FCSTD DOCUMENT  (FreeCAD 0.15R4671 (Git))
Label: OpenFacedCheeks
License: All rights reserved
LicenseURL: http://en.wikipedia.org/wiki/All_rights_reserved
objects: Sketcher::SketchObject×1
note: 1 computed .brp shape members not serialized (recipe doc carries the construction recipe); baked Part::Feature solids carry a one-line shape summary decoded from their .brp

FEATURE [Sketcher::SketchObject] Sketch
  sketch-geometry (18):
    g0: LineSegment StartX=0 StartY=0 StartZ=0 EndX=0 EndY=120.65 EndZ=0
    g1: LineSegment StartX=0 StartY=0 StartZ=0 EndX=285.75 EndY=0 EndZ=0
    g2: LineSegment StartX=285.75 StartY=0 StartZ=0 EndX=285.75 EndY=40.64 EndZ=0
    g3: LineSegment StartX=9.525 StartY=9.525 StartZ=0 EndX=276.225 EndY=9.525 EndZ=0
    g4: LineSegment StartX=9.525 StartY=9.525 StartZ=0 EndX=9.525 EndY=107.371 EndZ=0
    g5: LineSegment StartX=276.225 StartY=9.525 StartZ=0 EndX=276.225 EndY=34.925 EndZ=0
    g6: LineSegment StartX=276.225 StartY=34.925 StartZ=0 EndX=123.825 EndY=34.925 EndZ=0
    g7: LineSegment StartX=9.525 StartY=107.371 StartZ=0 EndX=17.241 EndY=101.786 EndZ=0
    g8: LineSegment StartX=17.241 StartY=101.786 StartZ=0 EndX=22.8257 EndY=109.502 EndZ=0
    g9: LineSegment StartX=22.8257 StartY=109.502 StartZ=0 EndX=89.6981 EndY=61.1019 EndZ=0
    g10: LineSegment StartX=89.6981 StartY=61.1019 StartZ=0 EndX=84.1134 EndY=53.3859 EndZ=0
    g11: LineSegment StartX=84.1134 StartY=53.3859 StartZ=0 EndX=94.4015 EndY=45.9397 EndZ=0
    g12: ArcOfCircle CenterX=12.7 CenterY=120.65 CenterZ=0 NormalX=0 NormalY=0 NormalZ=1 Radius=12.7 StartAngle=0.725088 EndAngle=3.14159
    g13: ArcOfCircle CenterX=266.7 CenterY=40.64 CenterZ=0 NormalX=0 NormalY=0 NormalZ=1 Radius=19.05 StartAngle=0 EndAngle=1.84657
    g14: ArcOfCircle CenterX=197.675 CenterY=284.558 CenterZ=0 NormalX=0 NormalY=0 NormalZ=1 Radius=234.447 StartAngle=3.86668 EndAngle=4.98816
    g15: LineSegment StartX=94.4015 StartY=45.9397 StartZ=0 EndX=100.358 EndY=54.1702 EndZ=0
    g16: LineSegment StartX=100.358 StartY=54.1702 StartZ=0 EndX=123.825 EndY=44.45 EndZ=0
    g17: LineSegment StartX=123.825 StartY=44.45 StartZ=0 EndX=123.825 EndY=34.925 EndZ=0
  constraints (56):
    c: Coincident(g0,g-1)
    c: PointOnObject(g0,g-2)
    c: Coincident(g1,g-1)
    c: Horizontal(g1)
    c: Coincident(g2,g1)
    c: Vertical(g2)
    c: Horizontal(g3)
    c: Coincident(g4,g3)
    c: Vertical(g4)
    c: Coincident(g5,g3)
    c: Vertical(g5)
    c: DistanceX(g-1,g3) = 9.525
    c: DistanceY(g-1,g3) = 9.525
    c: DistanceX(g3,g1) = 9.525
    c: DistanceY(g5,g3) = -25.4
    c: DistanceX(g3) = 266.7
    c: Coincident(g6,g5)
    c: Horizontal(g6)
    c: DistanceX(g6) = -152.4
    c: Coincident(g7,g4)
    c: Coincident(g7,g8)
    c: Coincident(g8,g9)
    c: Coincident(g9,g10)
    c: Coincident(g10,g11)
    c: Perpendicular(g10,g9)
    c: Perpendicular(g10,g11)
    c: Distance(g11) = 12.7
    c: Distance(g10) = 9.525
    c: Distance(g9) = 82.55
    c: Perpendicular(g9,g8)
    c: Perpendicular(g8,g7)
    c: Distance(g7) = 9.525
    c: Distance(g8) = 9.525
    c: Coincident(g12,g0)
    c: Coincident(g13,g2)
    c: Angle(g13,g2,g2) = 0
    c: Angle(g0,g12,g0) = -3.14159
    c: Radius(g12) = 12.7
    c: Radius(g13) = 19.05
    c: Coincident(g14,g13)
    c: Coincident(g14,g12)
    c: Angle(g14,g13,g13) = -3.14159
    c: Angle(g12,g14,g12) = -3.14159
    c: DistanceY(g0) = 120.65
    c: DistanceY(g2) = 40.64
    c: Radius(g14) = 234.447
    c: Coincident(g11,g15)
    c: Coincident(g15,g16)
    c: Coincident(g16,g17)
    c: Coincident(g17,g6)
    c: Vertical(g17)
    c: Angle(g16,g17) = 1.9635
    c: DistanceY(g17) = -9.525
    c: Perpendicular(g11,g15)
    c: Distance(g15) = 10.16
    c: Distance(g16) = 25.4
